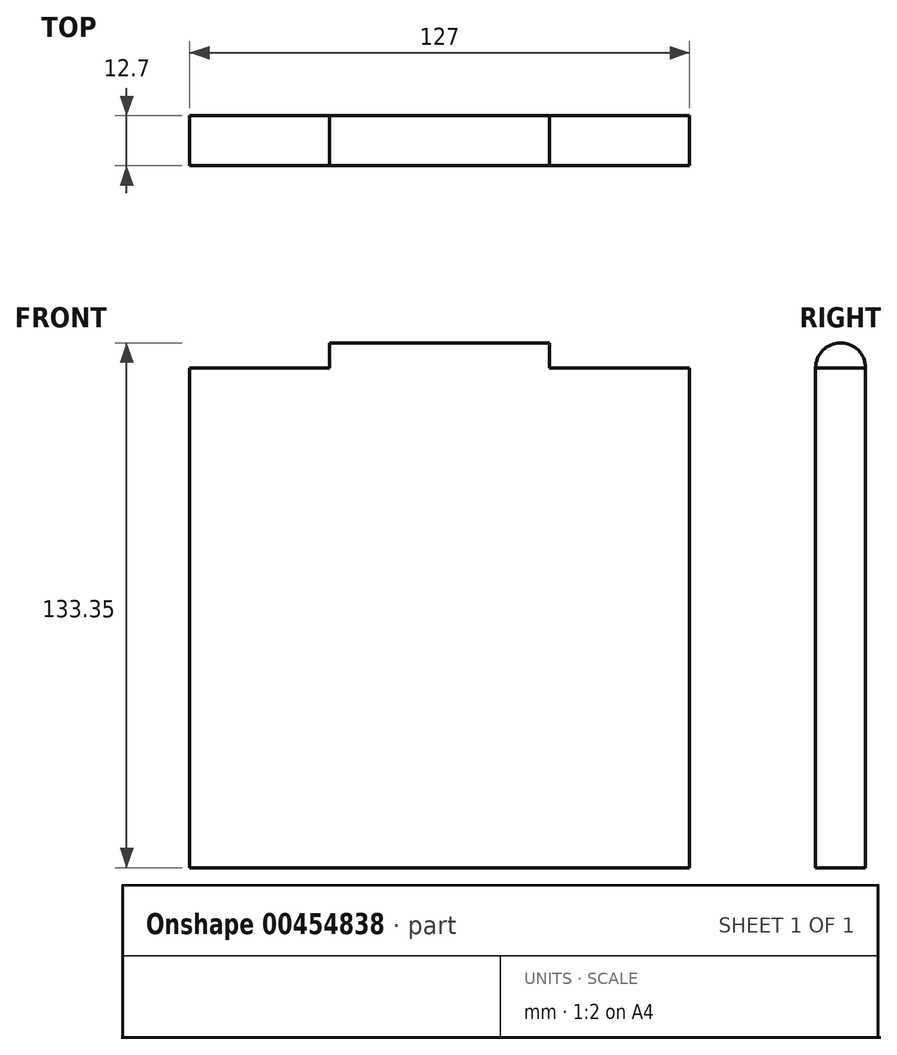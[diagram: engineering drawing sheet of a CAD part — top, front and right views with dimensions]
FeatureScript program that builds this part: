
annotation { "Feature Type Name" : "Feature", "Feature Type Description" : "" }
export const myFeature = defineFeature(function(context is Context, id is Id, definition is map)
    precondition{}
    {
        {
            var Q0;
            Q0=qCreatedBy(makeId("Front.planeOp"),FACE);
            var sketch = newSketch(context, id + "F0", { "sketchPlane" : qUnion([Q0])});
            skLineSegment(sketch, "E0.bottom", {"start": v(63.5, 63.5) * mm, "end": v(-63.5, 63.5) * mm});
            skLineSegment(sketch, "E0.top", {"start": v(63.5, -63.5) * mm, "end": v(-63.5, -63.5) * mm});
            skLineSegment(sketch, "E0.left", {"start": v(63.5, 63.5) * mm, "end": v(63.5, -63.5) * mm});
            skLineSegment(sketch, "E0.right", {"start": v(-63.5, 63.5) * mm, "end": v(-63.5, -63.5) * mm});
            skPoint(sketch, "E0.middle", {"position": v(0, 0) * mm});
            skSolve(sketch);
        }
        {
            var Q0;
            Q0 = qSketchRegion(id + "F0", true);
            extrude(context, id + "F1", {"entities" : qUnion([Q0]), "endBound" : BoundingType.SYMMETRIC, "depth" : 12.7 * mm, "offsetDistance" : 25.4 * mm});
        }
        {
            var Q0;
            Q0=qCreatedBy(makeId("Right.planeOp"),FACE);
            var sketch = newSketch(context, id + "F2", { "sketchPlane" : qUnion([Q0])});
            skCircle(sketch, "E1", {"center": v(0, 63.5) * mm, "radius": 6.35 * mm});
            skSolve(sketch);
        }
        {
            var Q0;
            Q0 = qSketchRegion(id + "F2", true);
            extrude(context, id + "F3", {"entities" : qUnion([Q0]), "operationType" : NewBodyOperationType.ADD, "endBound" : BoundingType.SYMMETRIC, "depth" : 55.88 * mm, "offsetDistance" : 25.4 * mm});
        }
    });
